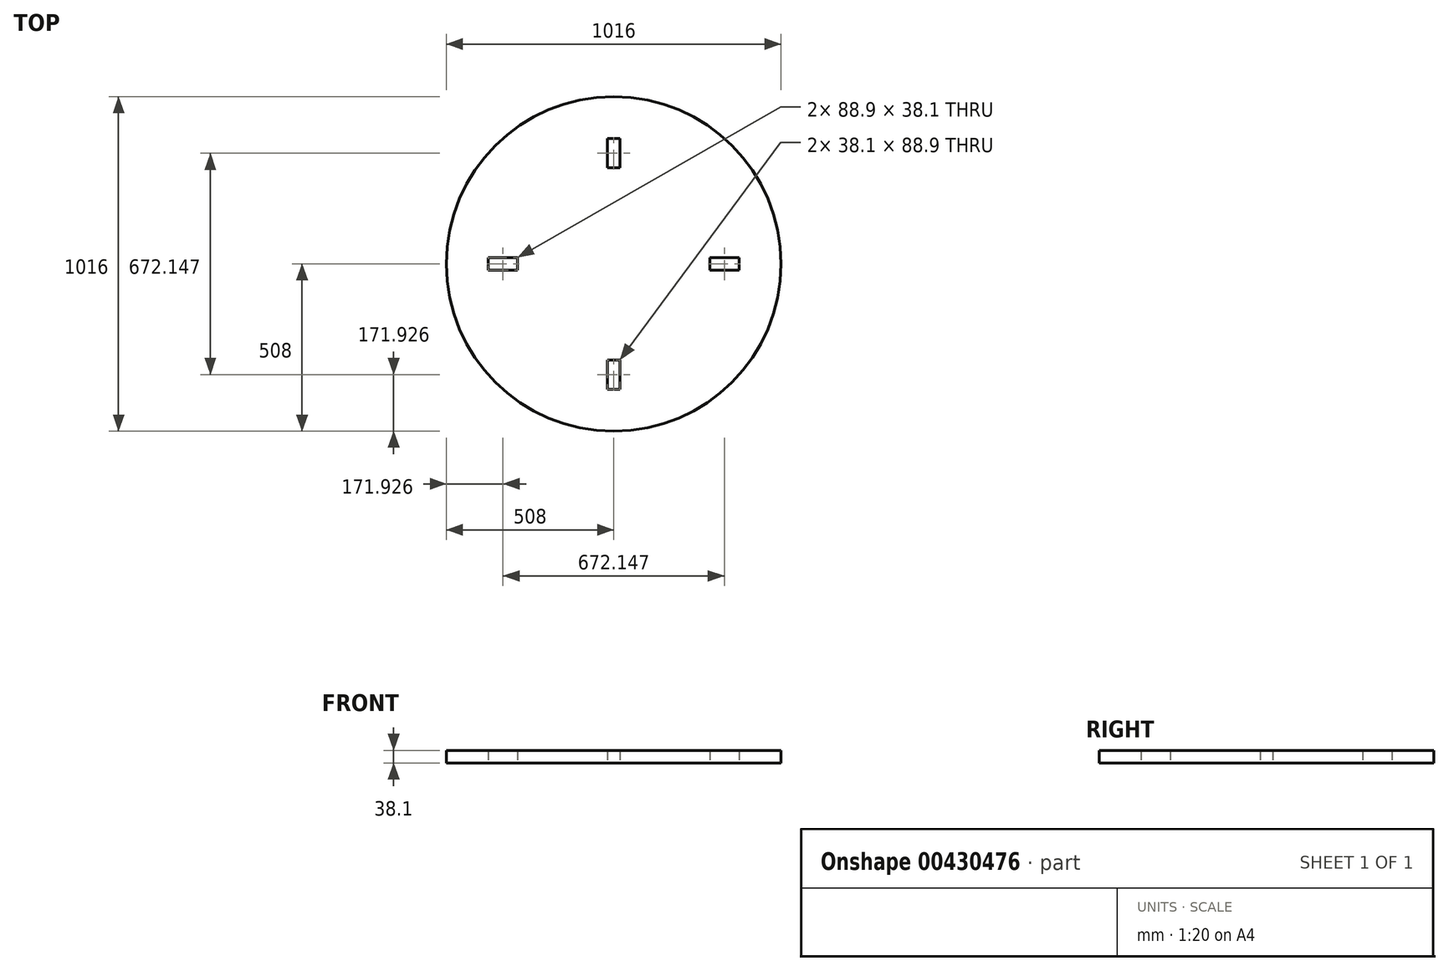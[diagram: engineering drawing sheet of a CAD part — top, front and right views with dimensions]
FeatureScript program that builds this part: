
annotation { "Feature Type Name" : "Feature", "Feature Type Description" : "" }
export const myFeature = defineFeature(function(context is Context, id is Id, definition is map)
    precondition{}
    {
        {
            var Q0;
            Q0=qCreatedBy(makeId("Top.planeOp"),FACE);
            var sketch = newSketch(context, id + "F0", { "sketchPlane" : qUnion([Q0])});
            skCircle(sketch, "E0", {"center": v(0, 0) * mm, "radius": 508 * mm});
            skSolve(sketch);
        }
        {
            var Q0;
            Q0 = qSketchRegion(id + "F0", true);
            extrude(context, id + "F1", {"entities" : qUnion([Q0]), "oppositeDirection" : true, "depth" : 38.1 * mm});
        }
        {
            var Q0;
            Q0=makeQuery(id+"F1.opExtrude","CAP_FACE",FACE,{"disambiguationData":[OSD([sQuery(id+"F0.wireOp",EDGE,"E0")])],"isStart":false});
            var sketch = newSketch(context, id + "F2", { "sketchPlane" : qUnion([Q0])});
            skCircle(sketch, "E1", {"center": v(0, 0) * mm, "radius": 381 * mm, "construction": true});
            skLineSegment(sketch, "E2.bottom", {"start": v(-19.05, 380.52) * mm, "end": v(19.05, 380.52) * mm});
            skLineSegment(sketch, "E2.top", {"start": v(-19.05, -380.52) * mm, "end": v(19.05, -380.52) * mm});
            skLineSegment(sketch, "E2.left", {"start": v(-19.05, 380.52) * mm, "end": v(-19.05, 291.62) * mm});
            skLineSegment(sketch, "E2.right", {"start": v(19.05, 380.52) * mm, "end": v(19.05, 291.62) * mm});
            skLineSegment(sketch, "E3", {"start": v(-19.05, 291.62) * mm, "end": v(19.05, 291.62) * mm});
            skLineSegment(sketch, "E4", {"start": v(-19.05, -291.62) * mm, "end": v(19.05, -291.62) * mm});
            skLineSegment(sketch, "E5.trimOffspring", {"start": v(-19.05, -291.62) * mm, "end": v(-19.05, -380.52) * mm});
            skLineSegment(sketch, "E6.trimOffspring", {"start": v(19.05, -291.62) * mm, "end": v(19.05, -380.52) * mm});
            skLineSegment(sketch, "E7", {"start": v(0, 0) * mm, "end": v(-269.4, 269.4) * mm, "construction": true});
            skLineSegment(sketch, "E8", {"start": v(0, 0) * mm, "end": v(0, 381) * mm, "construction": true});
            skLineSegment(sketch, "E9.MirrorCS", {"start": v(380.52, 19.05) * mm, "end": v(380.52, -19.05) * mm});
            skLineSegment(sketch, "E10.MirrorCS", {"start": v(291.62, 19.05) * mm, "end": v(291.62, -19.05) * mm});
            skLineSegment(sketch, "E11.MirrorCS", {"start": v(291.62, 19.05) * mm, "end": v(380.52, 19.05) * mm});
            skLineSegment(sketch, "E12.MirrorCS", {"start": v(291.62, -19.05) * mm, "end": v(380.52, -19.05) * mm});
            skLineSegment(sketch, "E13.MirrorCS", {"start": v(-291.62, 19.05) * mm, "end": v(-291.62, -19.05) * mm});
            skLineSegment(sketch, "E14.MirrorCS", {"start": v(-380.52, 19.05) * mm, "end": v(-380.52, -19.05) * mm});
            skLineSegment(sketch, "E15.MirrorCS", {"start": v(-380.52, -19.05) * mm, "end": v(-291.62, -19.05) * mm});
            skLineSegment(sketch, "E16.MirrorCS", {"start": v(-380.52, 19.05) * mm, "end": v(-291.62, 19.05) * mm});
            skSolve(sketch);
        }
        {
            var Q0;
            Q0=makeQuery(id+"F2.imprint","IMPRINT",FACE,{"disambiguationData":[TD([[makeQuery(id+"F2.imprint","IMPRINT",EDGE,{"derivedFrom":sQuery(id+"F2.wireOp",EDGE,"E13.MirrorCS")}),-1.0]])]});
            var Q1;
            Q1=makeQuery(id+"F2.imprint","IMPRINT",FACE,{"disambiguationData":[TD([[makeQuery(id+"F2.imprint","IMPRINT",EDGE,{"derivedFrom":sQuery(id+"F2.wireOp",EDGE,"E2.top")}),1.0]])]});
            var Q2;
            Q2=makeQuery(id+"F2.imprint","IMPRINT",FACE,{"disambiguationData":[TD([[makeQuery(id+"F2.imprint","IMPRINT",EDGE,{"derivedFrom":sQuery(id+"F2.wireOp",EDGE,"E9.MirrorCS")}),-1.0]])]});
            var Q3;
            Q3=makeQuery(id+"F2.imprint","IMPRINT",FACE,{"disambiguationData":[TD([[makeQuery(id+"F2.imprint","IMPRINT",EDGE,{"derivedFrom":sQuery(id+"F2.wireOp",EDGE,"E2.bottom")}),-1.0]])]});
            extrude(context, id + "F3", {"entities" : qUnion([Q0, Q1, Q2, Q3]), "operationType" : NewBodyOperationType.REMOVE, "endBound" : BoundingType.THROUGH_ALL, "oppositeDirection" : true, "depth" : 25.4 * mm});
        }
    });
